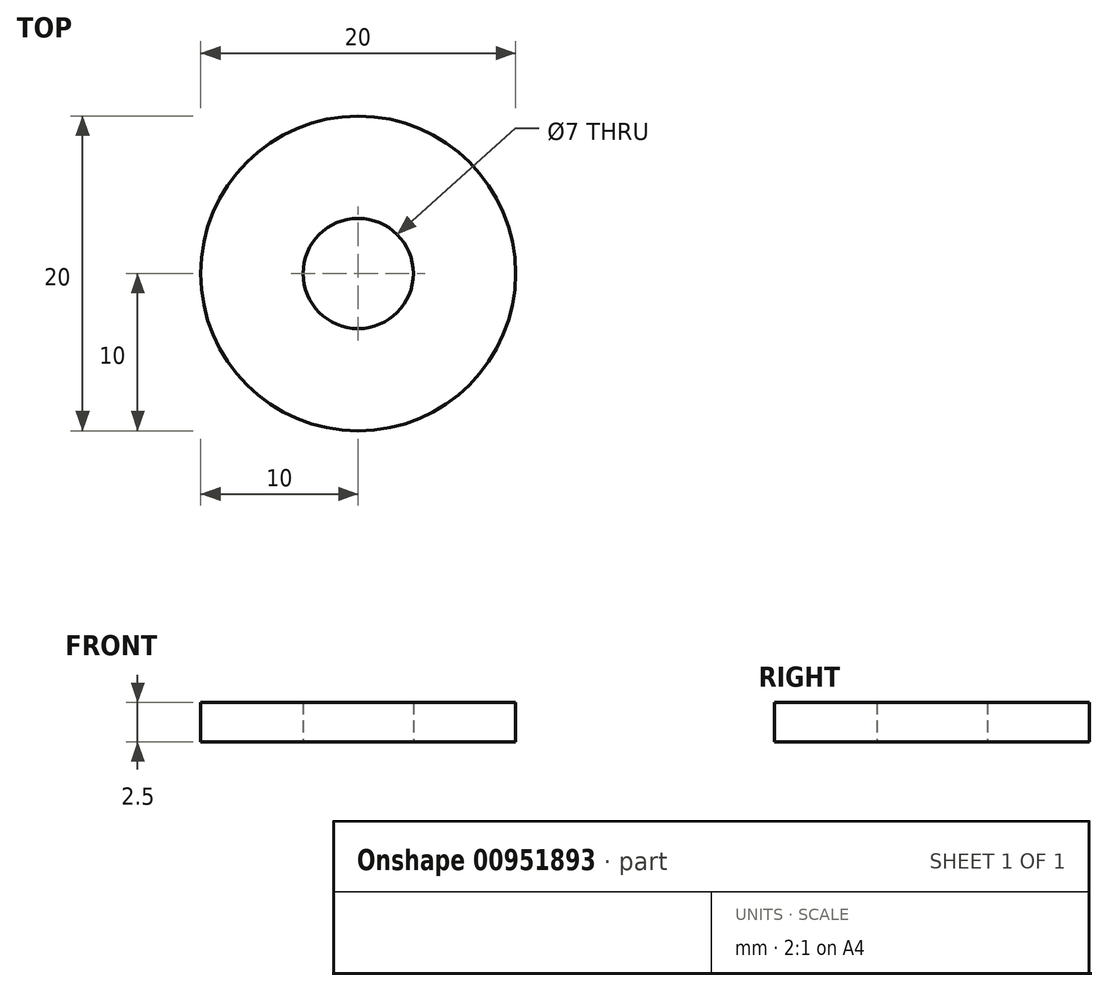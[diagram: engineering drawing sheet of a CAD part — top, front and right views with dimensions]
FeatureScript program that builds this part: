
annotation { "Feature Type Name" : "Feature", "Feature Type Description" : "" }
export const myFeature = defineFeature(function(context is Context, id is Id, definition is map)
    precondition{}
    {
        {
            var Q0;
            Q0=qCreatedBy(makeId("Top.planeOp"),FACE);
            var sketch = newSketch(context, id + "F0", { "sketchPlane" : qUnion([Q0])});
            skCircle(sketch, "E0", {"center": v(0, 0) * mm, "radius": 10 * mm});
            skCircle(sketch, "E1", {"center": v(0, 0) * mm, "radius": 3.5 * mm});
            skSolve(sketch);
        }
        {
            var Q0;
            Q0=makeQuery(id+"F0.imprint","IMPRINT",FACE,{"disambiguationData":[TD([[makeQuery(id+"F0.imprint","IMPRINT",EDGE,{"derivedFrom":sQuery(id+"F0.wireOp",EDGE,"E0")}),1.0]])]});
            extrude(context, id + "F1", {"entities" : qUnion([Q0]), "depth" : 2.5 * mm, "offsetDistance" : 25 * mm});
        }
    });
